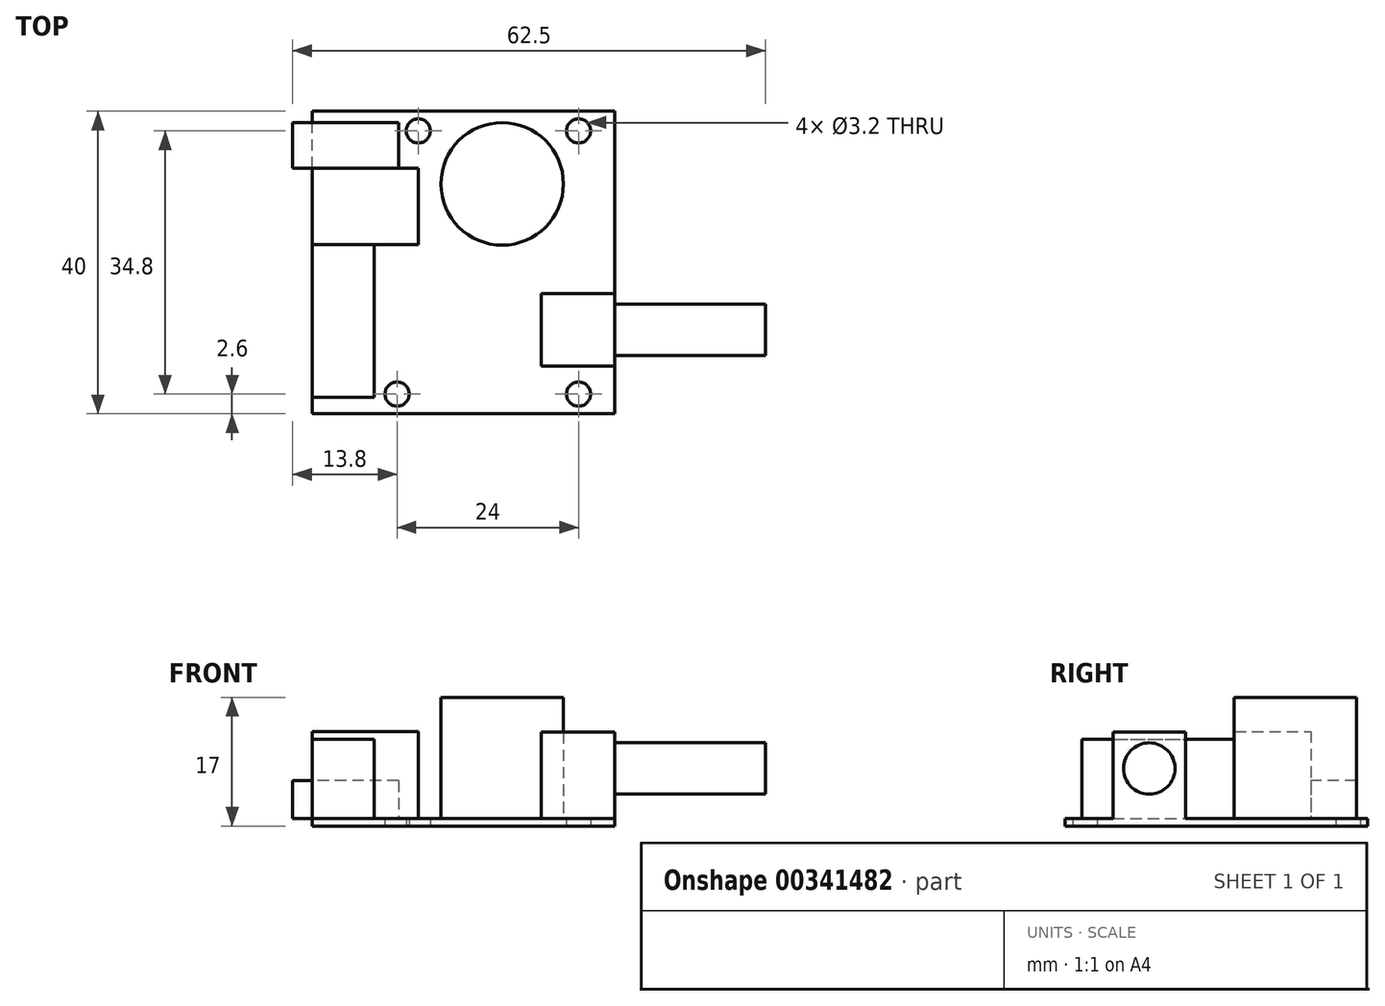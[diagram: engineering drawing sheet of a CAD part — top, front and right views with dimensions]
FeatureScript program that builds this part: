
annotation { "Feature Type Name" : "Feature", "Feature Type Description" : "" }
export const myFeature = defineFeature(function(context is Context, id is Id, definition is map)
    precondition{}
    {
        {
            var Q0;
            Q0=qCreatedBy(makeId("Top.planeOp"),FACE);
            var sketch = newSketch(context, id + "F0", { "sketchPlane" : qUnion([Q0])});
            skLineSegment(sketch, "E0.bottom", {"start": v(20, -20) * mm, "end": v(-20, -20) * mm});
            skLineSegment(sketch, "E0.top", {"start": v(20, 20) * mm, "end": v(-20, 20) * mm});
            skLineSegment(sketch, "E0.left", {"start": v(20, -20) * mm, "end": v(20, 20) * mm});
            skLineSegment(sketch, "E0.right", {"start": v(-20, -20) * mm, "end": v(-20, 20) * mm});
            skPoint(sketch, "E0.middle", {"position": v(0, 0) * mm});
            skCircle(sketch, "E1", {"center": v(-6, 17.4) * mm, "radius": 1.6 * mm});
            skCircle(sketch, "E2", {"center": v(15.2, 17.4) * mm, "radius": 1.6 * mm});
            skCircle(sketch, "E3", {"center": v(-8.8, -17.4) * mm, "radius": 1.6 * mm});
            skCircle(sketch, "E4", {"center": v(15.2, -17.4) * mm, "radius": 1.6 * mm});
            skSolve(sketch);
        }
        {
            var Q0;
            Q0 = qSketchRegion(id + "F0", true);
            extrude(context, id + "F1", {"entities" : qUnion([Q0]), "depth" : 1 * mm});
        }
        {
            var Q0;
            Q0=makeQuery(id+"F1.opExtrude","CAP_FACE",FACE,{"disambiguationData":[OSD([sQuery(id+"F0.wireOp",EDGE,"E0.bottom"),sQuery(id+"F0.wireOp",EDGE,"E0.top"),sQuery(id+"F0.wireOp",EDGE,"E0.left"),sQuery(id+"F0.wireOp",EDGE,"E0.right"),sQuery(id+"F0.wireOp",EDGE,"E1"),sQuery(id+"F0.wireOp",EDGE,"E2"),sQuery(id+"F0.wireOp",EDGE,"E3"),sQuery(id+"F0.wireOp",EDGE,"E4")])],"isStart":false});
            var sketch = newSketch(context, id + "F2", { "sketchPlane" : qUnion([Q0])});
            skLineSegment(sketch, "E5.bottom", {"start": v(20, -13.7) * mm, "end": v(10.3, -13.7) * mm});
            skLineSegment(sketch, "E5.top", {"start": v(20, -4.1) * mm, "end": v(10.3, -4.1) * mm});
            skLineSegment(sketch, "E5.left", {"start": v(20, -13.7) * mm, "end": v(20, -4.1) * mm});
            skLineSegment(sketch, "E5.right", {"start": v(10.3, -13.7) * mm, "end": v(10.3, -4.1) * mm});
            skSolve(sketch);
        }
        {
            var Q0;
            Q0 = qSketchRegion(id + "F2", true);
            extrude(context, id + "F3", {"entities" : qUnion([Q0]), "operationType" : NewBodyOperationType.ADD, "depth" : 11.4 * mm});
        }
        {
            var Q0;
            Q0=makeQuery(id+"F3.boolean.opBoolean","MERGE",FACE,{"derivedFrom":[makeQuery(id+"F1.opExtrude","SWEPT_FACE",FACE,{"disambiguationData":[OSD([sQuery(id+"F0.wireOp",EDGE,"E0.left")])]}),makeQuery(id+"F3.opExtrude","SWEPT_FACE",FACE,{"disambiguationData":[OSD([sQuery(id+"F2.wireOp",EDGE,"E5.left")])]})]});
            var sketch = newSketch(context, id + "F4", { "sketchPlane" : qUnion([Q0])});
            skCircle(sketch, "E6", {"center": v(-8.9, 7.6) * mm, "radius": 3.4 * mm});
            skPoint(sketch, "E6.centerSnap0", {"position": v(-8.9, 12.4) * mm});
            skSolve(sketch);
        }
        {
            var Q0;
            Q0 = qSketchRegion(id + "F4", true);
            extrude(context, id + "F5", {"entities" : qUnion([Q0]), "operationType" : NewBodyOperationType.ADD, "depth" : 19.9 * mm});
        }
        {
            var Q0;
            Q0=makeQuery(id+"F1.opExtrude","CAP_FACE",FACE,{"disambiguationData":[OSD([sQuery(id+"F0.wireOp",EDGE,"E0.bottom"),sQuery(id+"F0.wireOp",EDGE,"E0.top"),sQuery(id+"F0.wireOp",EDGE,"E0.left"),sQuery(id+"F0.wireOp",EDGE,"E0.right"),sQuery(id+"F0.wireOp",EDGE,"E1"),sQuery(id+"F0.wireOp",EDGE,"E2"),sQuery(id+"F0.wireOp",EDGE,"E3"),sQuery(id+"F0.wireOp",EDGE,"E4")])],"isStart":false});
            var sketch = newSketch(context, id + "F6", { "sketchPlane" : qUnion([Q0])});
            skCircle(sketch, "E7", {"center": v(5.1, 10.4) * mm, "radius": 8.1 * mm});
            skSolve(sketch);
        }
        {
            var Q0;
            Q0 = qSketchRegion(id + "F6", true);
            extrude(context, id + "F7", {"entities" : qUnion([Q0]), "operationType" : NewBodyOperationType.ADD, "depth" : 16 * mm});
        }
        {
            var Q0;
            Q0=makeQuery(id+"F1.opExtrude","CAP_FACE",FACE,{"disambiguationData":[OSD([sQuery(id+"F0.wireOp",EDGE,"E0.bottom"),sQuery(id+"F0.wireOp",EDGE,"E0.top"),sQuery(id+"F0.wireOp",EDGE,"E0.left"),sQuery(id+"F0.wireOp",EDGE,"E0.right"),sQuery(id+"F0.wireOp",EDGE,"E1"),sQuery(id+"F0.wireOp",EDGE,"E2"),sQuery(id+"F0.wireOp",EDGE,"E3"),sQuery(id+"F0.wireOp",EDGE,"E4")])],"isStart":false});
            var sketch = newSketch(context, id + "F8", { "sketchPlane" : qUnion([Q0])});
            skLineSegment(sketch, "E8.bottom", {"start": v(-8.6, 18.5) * mm, "end": v(-22.6, 18.5) * mm});
            skLineSegment(sketch, "E8.top", {"start": v(-8.6, 12.5) * mm, "end": v(-22.6, 12.5) * mm});
            skLineSegment(sketch, "E8.left", {"start": v(-8.6, 18.5) * mm, "end": v(-8.6, 12.5) * mm});
            skLineSegment(sketch, "E8.right", {"start": v(-22.6, 18.5) * mm, "end": v(-22.6, 12.5) * mm});
            skSolve(sketch);
        }
        {
            var Q0;
            Q0 = qSketchRegion(id + "F8", true);
            extrude(context, id + "F9", {"entities" : qUnion([Q0]), "operationType" : NewBodyOperationType.ADD, "depth" : 5 * mm});
        }
        {
            var Q0;
            Q0=makeQuery(id+"F1.opExtrude","CAP_FACE",FACE,{"disambiguationData":[OSD([sQuery(id+"F0.wireOp",EDGE,"E0.bottom"),sQuery(id+"F0.wireOp",EDGE,"E0.top"),sQuery(id+"F0.wireOp",EDGE,"E0.left"),sQuery(id+"F0.wireOp",EDGE,"E0.right"),sQuery(id+"F0.wireOp",EDGE,"E1"),sQuery(id+"F0.wireOp",EDGE,"E2"),sQuery(id+"F0.wireOp",EDGE,"E3"),sQuery(id+"F0.wireOp",EDGE,"E4")])],"isStart":false});
            var sketch = newSketch(context, id + "F10", { "sketchPlane" : qUnion([Q0])});
            skLineSegment(sketch, "E9.bottom", {"start": v(-20, -17.8) * mm, "end": v(-11.8, -17.8) * mm});
            skLineSegment(sketch, "E9.top", {"start": v(-20, 2.4) * mm, "end": v(-11.8, 2.4) * mm});
            skLineSegment(sketch, "E9.left", {"start": v(-20, -17.8) * mm, "end": v(-20, 2.4) * mm});
            skLineSegment(sketch, "E9.right", {"start": v(-11.8, -17.8) * mm, "end": v(-11.8, 2.4) * mm});
            skSolve(sketch);
        }
        {
            var Q0;
            Q0 = qSketchRegion(id + "F10", true);
            extrude(context, id + "F11", {"entities" : qUnion([Q0]), "operationType" : NewBodyOperationType.ADD, "depth" : 10.5 * mm});
        }
        {
            var Q0;
            Q0=makeQuery(id+"F1.opExtrude","CAP_FACE",FACE,{"disambiguationData":[OSD([sQuery(id+"F0.wireOp",EDGE,"E0.bottom"),sQuery(id+"F0.wireOp",EDGE,"E0.top"),sQuery(id+"F0.wireOp",EDGE,"E0.left"),sQuery(id+"F0.wireOp",EDGE,"E0.right"),sQuery(id+"F0.wireOp",EDGE,"E1"),sQuery(id+"F0.wireOp",EDGE,"E2"),sQuery(id+"F0.wireOp",EDGE,"E3"),sQuery(id+"F0.wireOp",EDGE,"E4")])],"isStart":false});
            var sketch = newSketch(context, id + "F12", { "sketchPlane" : qUnion([Q0])});
            skLineSegment(sketch, "E10.bottom", {"start": v(-20, 2.4) * mm, "end": v(-6, 2.4) * mm});
            skLineSegment(sketch, "E10.top", {"start": v(-20, 12.5) * mm, "end": v(-6, 12.5) * mm});
            skLineSegment(sketch, "E10.left", {"start": v(-20, 2.4) * mm, "end": v(-20, 12.5) * mm});
            skLineSegment(sketch, "E10.right", {"start": v(-6, 2.4) * mm, "end": v(-6, 12.5) * mm});
            skSolve(sketch);
        }
        {
            var Q0;
            Q0 = qSketchRegion(id + "F12", true);
            extrude(context, id + "F13", {"entities" : qUnion([Q0]), "operationType" : NewBodyOperationType.ADD, "depth" : 11.5 * mm});
        }
    });
